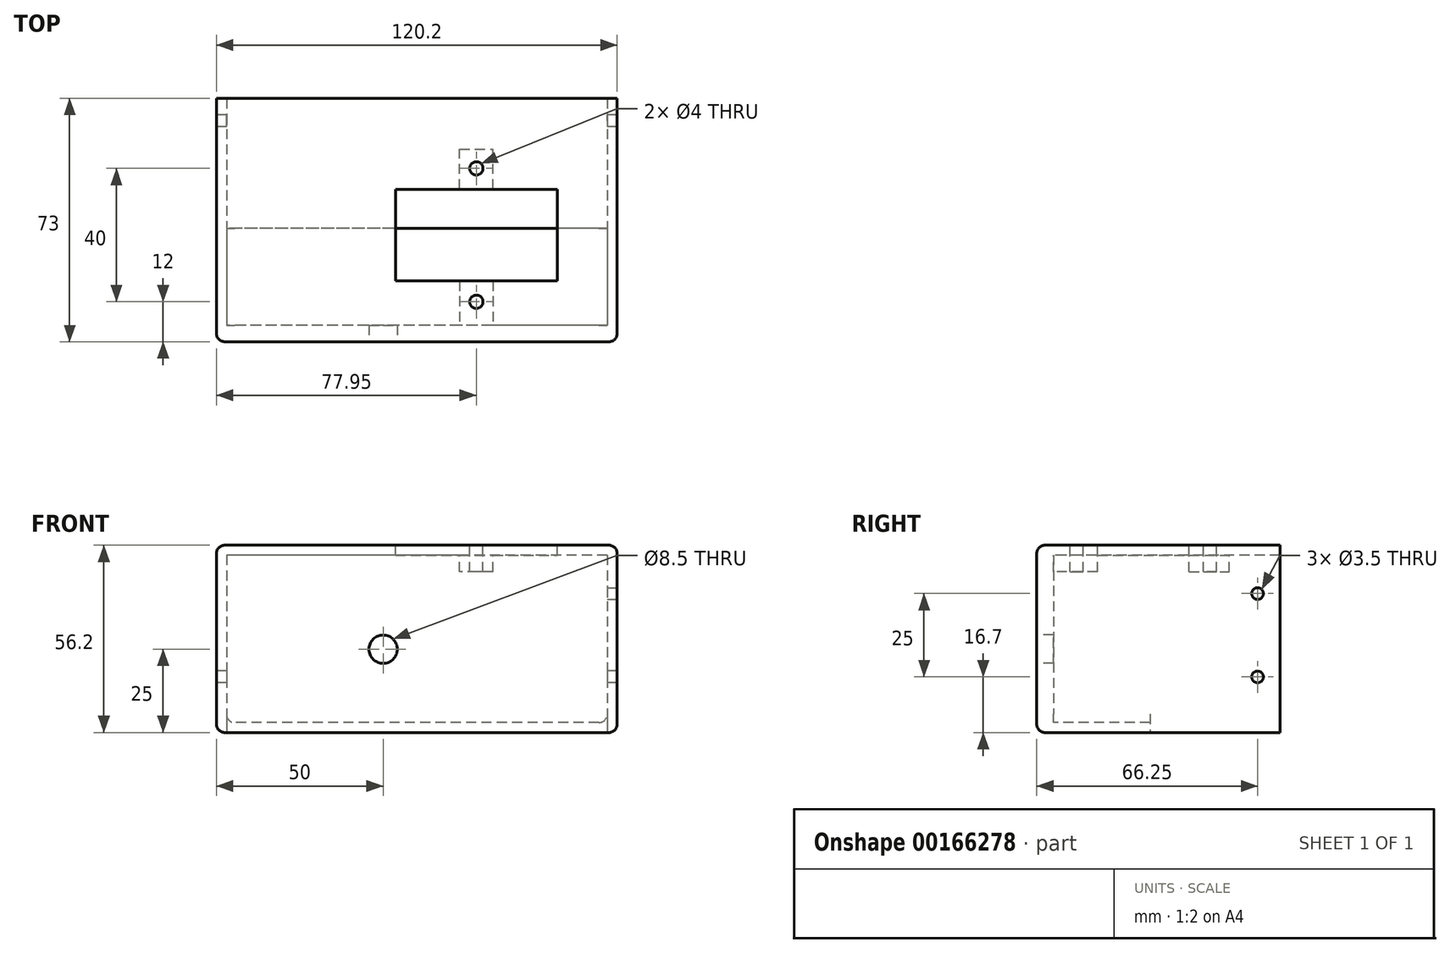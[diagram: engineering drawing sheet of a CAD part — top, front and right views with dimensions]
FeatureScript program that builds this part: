
annotation { "Feature Type Name" : "Feature", "Feature Type Description" : "" }
export const myFeature = defineFeature(function(context is Context, id is Id, definition is map)
    precondition{}
    {
        {
            var Q0;
            Q0=qCreatedBy(makeId("Front.planeOp"),FACE);
            var sketch = newSketch(context, id + "F0", { "sketchPlane" : qUnion([Q0])});
            skLineSegment(sketch, "E0.bottom", {"start": v(60.1, 28.1) * mm, "end": v(-60.1, 28.1) * mm});
            skLineSegment(sketch, "E0.top", {"start": v(60.1, -28.1) * mm, "end": v(-60.1, -28.1) * mm});
            skLineSegment(sketch, "E0.left", {"start": v(60.1, 28.1) * mm, "end": v(60.1, -28.1) * mm});
            skLineSegment(sketch, "E0.right", {"start": v(-60.1, 28.1) * mm, "end": v(-60.1, -28.1) * mm});
            skPoint(sketch, "E0.middle", {"position": v(0, 0) * mm});
            skCircle(sketch, "E1", {"center": v(-10.1, -3.1) * mm, "radius": 4.25 * mm});
            skSolve(sketch);
        }
        {
            var Q0;
            Q0=makeQuery(id+"F0.imprint","IMPRINT",FACE,{"disambiguationData":[TD([[makeQuery(id+"F0.imprint","IMPRINT",EDGE,{"derivedFrom":sQuery(id+"F0.wireOp",EDGE,"E0.bottom")}),1.0]])]});
            extrude(context, id + "F1", {"entities" : qUnion([Q0]), "oppositeDirection" : true, "depth" : 5 * mm});
        }
        {
            var Q0;
            Q0=makeQuery(id+"F1.opExtrude","CAP_FACE",FACE,{"disambiguationData":[OSD([sQuery(id+"F0.wireOp",EDGE,"E0.bottom"),sQuery(id+"F0.wireOp",EDGE,"E0.top"),sQuery(id+"F0.wireOp",EDGE,"E0.left"),sQuery(id+"F0.wireOp",EDGE,"E0.right"),sQuery(id+"F0.wireOp",EDGE,"E1")])],"isStart":false});
            var sketch = newSketch(context, id + "F2", { "sketchPlane" : qUnion([Q0])});
            skLineSegment(sketch, "E2.0", {"start": v(-60.1, 28.1) * mm, "end": v(60.1, 28.1) * mm});
            skLineSegment(sketch, "E3.0", {"start": v(-60.1, 28.1) * mm, "end": v(-60.1, -28.1) * mm});
            skLineSegment(sketch, "E4.0", {"start": v(-60.1, -28.1) * mm, "end": v(60.1, -28.1) * mm});
            skLineSegment(sketch, "E5.0", {"start": v(60.1, 28.1) * mm, "end": v(60.1, -28.1) * mm});
            skLineSegment(sketch, "E6.0", {"start": v(-57.1, 25.1) * mm, "end": v(57.1, 25.1) * mm});
            skLineSegment(sketch, "E6.1", {"start": v(-57.1, 25.1) * mm, "end": v(-57.1, -25.1) * mm});
            skLineSegment(sketch, "E6.2", {"start": v(-57.1, -25.1) * mm, "end": v(57.1, -25.1) * mm});
            skLineSegment(sketch, "E6.3", {"start": v(57.1, 25.1) * mm, "end": v(57.1, -25.1) * mm});
            skSolve(sketch);
        }
        {
            var Q0;
            Q0=makeQuery(id+"F2.imprint","IMPRINT",FACE,{"disambiguationData":[TD([[makeQuery(id+"F2.imprint","IMPRINT",EDGE,{"derivedFrom":sQuery(id+"F2.wireOp",EDGE,"E2.0")}),-1.0]])]});
            extrude(context, id + "F3", {"entities" : qUnion([Q0]), "operationType" : NewBodyOperationType.ADD, "depth" : (60 + 3 + 5) * mm});
        }
        {
            var Q0;
            Q0=makeQuery(id+"F3.boolean.opBoolean","MERGE",FACE,{"derivedFrom":[makeQuery(id+"F1.opExtrude","SWEPT_FACE",FACE,{"disambiguationData":[OSD([sQuery(id+"F0.wireOp",EDGE,"E0.bottom")])]}),makeQuery(id+"F3.opExtrude","SWEPT_FACE",FACE,{"disambiguationData":[OSD([sQuery(id+"F2.wireOp",EDGE,"E2.0")])]})]});
            var sketch = newSketch(context, id + "F4", { "sketchPlane" : qUnion([Q0])});
            skLineSegment(sketch, "E7.bottom", {"start": v(-6.4, 18.25) * mm, "end": v(42.1, 18.25) * mm});
            skLineSegment(sketch, "E7.top", {"start": v(-6.4, 45.75) * mm, "end": v(42.1, 45.75) * mm});
            skLineSegment(sketch, "E7.left", {"start": v(-6.4, 18.25) * mm, "end": v(-6.4, 45.75) * mm});
            skLineSegment(sketch, "E7.right", {"start": v(42.1, 18.25) * mm, "end": v(42.1, 45.75) * mm});
            skPoint(sketch, "E7.middle", {"position": v(17.85, 32) * mm});
            skCircle(sketch, "E8", {"center": v(17.85, 52) * mm, "radius": 2 * mm});
            skCircle(sketch, "E9", {"center": v(17.85, 12) * mm, "radius": 2 * mm});
            skLineSegment(sketch, "E10", {"start": v(17.85, 12) * mm, "end": v(17.85, 52) * mm, "construction": true});
            skLineSegment(sketch, "E11", {"start": v(42.1, 32) * mm, "end": v(-6.4, 32) * mm, "construction": true});
            skLineSegment(sketch, "E12.0", {"start": v(57.1, 5) * mm, "end": v(-57.1, 5) * mm, "construction": true});
            skLineSegment(sketch, "E13.0", {"start": v(57.1, 73) * mm, "end": v(57.1, 5) * mm, "construction": true});
            skSolve(sketch);
        }
        {
            var Q0;
            Q0 = qSketchRegion(id + "F4", true);
            extrude(context, id + "F5", {"entities" : qUnion([Q0]), "operationType" : NewBodyOperationType.REMOVE, "oppositeDirection" : true, "depth" : 25 * mm});
        }
        {
            var Q0;
            Q0=makeQuery(id+"F3.boolean.opBoolean","MERGE",FACE,{"derivedFrom":[makeQuery(id+"F1.opExtrude","SWEPT_FACE",FACE,{"disambiguationData":[OSD([sQuery(id+"F0.wireOp",EDGE,"E0.right")])]}),makeQuery(id+"F3.opExtrude","SWEPT_FACE",FACE,{"disambiguationData":[OSD([sQuery(id+"F2.wireOp",EDGE,"E5.0")])]})]});
            var sketch = newSketch(context, id + "F6", { "sketchPlane" : qUnion([Q0])});
            skLineSegment(sketch, "E14.0", {"start": v(-73, 25.1) * mm, "end": v(-5, 25.1) * mm, "construction": true});
            skCircle(sketch, "E15", {"center": v(-66.25, -11.4) * mm, "radius": 1.75 * mm});
            skSolve(sketch);
        }
        {
            var Q0;
            Q0=makeQuery(id+"F6.imprint","IMPRINT",FACE,{"disambiguationData":[TD([[makeQuery(id+"F6.imprint","IMPRINT",EDGE,{"derivedFrom":sQuery(id+"F6.wireOp",EDGE,"E15")}),1.0]])]});
            extrude(context, id + "F7", {"entities" : qUnion([Q0]), "operationType" : NewBodyOperationType.REMOVE, "endBound" : BoundingType.THROUGH_ALL, "oppositeDirection" : true, "depth" : 25 * mm});
        }
        {
            var Q0;
            Q0=makeQuery(id+"F3.boolean.opBoolean","MERGE",FACE,{"derivedFrom":[makeQuery(id+"F1.opExtrude","SWEPT_FACE",FACE,{"disambiguationData":[OSD([sQuery(id+"F0.wireOp",EDGE,"E0.left")])]}),makeQuery(id+"F3.opExtrude","SWEPT_FACE",FACE,{"disambiguationData":[OSD([sQuery(id+"F2.wireOp",EDGE,"E3.0")])]})]});
            var sketch = newSketch(context, id + "F8", { "sketchPlane" : qUnion([Q0])});
            skCircle(sketch, "E16.0", {"center": v(66.25, -11.4) * mm, "radius": 1.75 * mm, "construction": true});
            skLineSegment(sketch, "E17", {"start": v(66.25, -11.4) * mm, "end": v(66.25, 28.1) * mm, "construction": true});
            skLineSegment(sketch, "E18.0", {"start": v(73, 25.1) * mm, "end": v(5, 25.1) * mm, "construction": true});
            skCircle(sketch, "E19", {"center": v(66.25, 13.6) * mm, "radius": 1.75 * mm});
            skSolve(sketch);
        }
        {
            var Q0;
            Q0=makeQuery(id+"F8.imprint","IMPRINT",FACE,{"disambiguationData":[TD([[makeQuery(id+"F8.imprint","IMPRINT",EDGE,{"derivedFrom":sQuery(id+"F8.wireOp",EDGE,"E19")}),1.0]])]});
            var Q1;
            Q1=makeQuery(id+"F3.opExtrude","SWEPT_FACE",FACE,{"disambiguationData":[OSD([sQuery(id+"F2.wireOp",EDGE,"E6.1")])]});
            extrude(context, id + "F9", {"entities" : qUnion([Q0]), "operationType" : NewBodyOperationType.REMOVE, "endBound" : BoundingType.UP_TO_SURFACE, "oppositeDirection" : true, "endBoundEntityFace" : qUnion([Q1]), "depth" : 25 * mm});
        }
        {
            var Q0;
            Q0=makeQuery(id+"F3.boolean.opBoolean","MERGE",FACE,{"derivedFrom":[makeQuery(id+"F1.opExtrude","SWEPT_FACE",FACE,{"disambiguationData":[OSD([sQuery(id+"F0.wireOp",EDGE,"E0.top")])]}),makeQuery(id+"F3.opExtrude","SWEPT_FACE",FACE,{"disambiguationData":[OSD([sQuery(id+"F2.wireOp",EDGE,"E4.0")])]})]});
            var sketch = newSketch(context, id + "F10", { "sketchPlane" : qUnion([Q0])});
            skLineSegment(sketch, "E20.0", {"start": v(57.1, -73) * mm, "end": v(57.1, -34) * mm});
            skLineSegment(sketch, "E21.0", {"start": v(-57.1, -73) * mm, "end": v(-57.1, -34) * mm});
            skLineSegment(sketch, "E22", {"start": v(57.1, -34) * mm, "end": v(-57.1, -34) * mm});
            skLineSegment(sketch, "E23", {"start": v(-57.1, -73) * mm, "end": v(57.1, -73) * mm});
            skPoint(sketch, "E24.orphan", {"position": v(57.1, -5) * mm});
            skPoint(sketch, "E25.orphan", {"position": v(-57.1, -5) * mm});
            skSolve(sketch);
        }
        {
            var Q0;
            Q0=makeQuery(id+"F10.imprint","IMPRINT",FACE,{"disambiguationData":[TD([[makeQuery(id+"F10.imprint","IMPRINT",EDGE,{"derivedFrom":sQuery(id+"F10.wireOp",EDGE,"E20.0")}),1.0]])]});
            var Q1;
            Q1=makeQuery(id+"F3.opExtrude","SWEPT_FACE",FACE,{"disambiguationData":[OSD([sQuery(id+"F2.wireOp",EDGE,"E6.2")])]});
            extrude(context, id + "F11", {"entities" : qUnion([Q0]), "operationType" : NewBodyOperationType.REMOVE, "endBound" : BoundingType.UP_TO_SURFACE, "oppositeDirection" : true, "endBoundEntityFace" : qUnion([Q1]), "depth" : 25 * mm});
        }
        {
            var Q0;
            Q0=makeQuery(id+"F3.boolean.opBoolean","MERGE",FACE,{"derivedFrom":[makeQuery(id+"F1.opExtrude","SWEPT_FACE",FACE,{"disambiguationData":[OSD([sQuery(id+"F0.wireOp",EDGE,"E0.bottom")])]}),makeQuery(id+"F3.opExtrude","SWEPT_FACE",FACE,{"disambiguationData":[OSD([sQuery(id+"F2.wireOp",EDGE,"E2.0")])]})]});
            var sketch = newSketch(context, id + "F12", { "sketchPlane" : qUnion([Q0])});
            skText(sketch, "E26", { "text": "TJL Engineering", "fontName": "RobotoSlab-Bold.ttf"});
            const initialGuessF12  = {"E26": [-0.0551, -0.0231, 1, 0, 0.00546]};
            skSetInitialGuess(sketch, initialGuessF12);
            skSolve(sketch);
        }
        {
            var Q0;
            Q0 = qSketchRegion(id + "F12", true);
            extrude(context, id + "F13", {"entities" : qUnion([Q0]), "operationType" : NewBodyOperationType.REMOVE, "oppositeDirection" : true, "depth" : 2 * mm});
        }
        {
            var Q0;
            Q0=makeQuery(id+"F3.opExtrude","SWEPT_FACE",FACE,{"disambiguationData":[OSD([sQuery(id+"F2.wireOp",EDGE,"E6.0")])]});
            var sketch = newSketch(context, id + "F14", { "sketchPlane" : qUnion([Q0])});
            skCircle(sketch, "E27.0", {"center": v(17.85, -52) * mm, "radius": 2 * mm, "construction": true});
            skCircle(sketch, "E27.1", {"center": v(17.85, -12) * mm, "radius": 2 * mm, "construction": true});
            skLineSegment(sketch, "E28", {"start": v(-6.4, -32) * mm, "end": v(42.1, -32) * mm, "construction": true});
            skLineSegment(sketch, "E29", {"start": v(17.85, -45.75) * mm, "end": v(17.85, -57.75) * mm, "construction": true});
            skLineSegment(sketch, "E30.0", {"start": v(12.85, -45.75) * mm, "end": v(12.85, -57.75) * mm});
            skLineSegment(sketch, "E31.0", {"start": v(22.85, -45.75) * mm, "end": v(22.85, -57.75) * mm});
            skLineSegment(sketch, "E32", {"start": v(12.85, -57.75) * mm, "end": v(22.85, -57.75) * mm});
            skLineSegment(sketch, "E33.MirrorCS", {"start": v(12.85, -18.25) * mm, "end": v(12.85, -6.25) * mm});
            skLineSegment(sketch, "E34.MirrorCS", {"start": v(17.85, -18.25) * mm, "end": v(17.85, -6.25) * mm, "construction": true});
            skLineSegment(sketch, "E35.MirrorCS", {"start": v(22.85, -18.25) * mm, "end": v(22.85, -6.25) * mm});
            skLineSegment(sketch, "E36", {"start": v(12.85, -45.75) * mm, "end": v(22.85, -45.75) * mm});
            skLineSegment(sketch, "E37", {"start": v(12.85, -18.25) * mm, "end": v(22.85, -18.25) * mm});
            skLineSegment(sketch, "E38", {"start": v(12.85, -6.25) * mm, "end": v(12.85, -5) * mm});
            skLineSegment(sketch, "E39", {"start": v(12.85, -5) * mm, "end": v(22.85, -5) * mm});
            skLineSegment(sketch, "E40", {"start": v(22.85, -5) * mm, "end": v(22.85, -6.25) * mm});
            skCircle(sketch, "E41", {"center": v(17.85, -52) * mm, "radius": 1.9 * mm});
            skCircle(sketch, "E42", {"center": v(17.85, -12) * mm, "radius": 1.9 * mm});
            skSolve(sketch);
        }
        {
            var Q0;
            Q0=makeQuery(id+"F14.imprint","IMPRINT",FACE,{"disambiguationData":[TD([[makeQuery(id+"F14.imprint","IMPRINT",EDGE,{"derivedFrom":sQuery(id+"F14.wireOp",EDGE,"E30.0")}),1.0]])]});
            var Q1;
            Q1=makeQuery(id+"F14.imprint","IMPRINT",FACE,{"disambiguationData":[TD([[makeQuery(id+"F14.imprint","IMPRINT",EDGE,{"derivedFrom":sQuery(id+"F14.wireOp",EDGE,"E33.MirrorCS")}),-1.0]])]});
            extrude(context, id + "F15", {"entities" : qUnion([Q0, Q1]), "operationType" : NewBodyOperationType.ADD, "depth" : 5 * mm});
        }
        {
            var Q0;
            Q0=makeQuery(id+"F3.boolean.opBoolean","MERGE",EDGE,{"derivedFrom":[makeQuery(id+"F1.opExtrude","SWEPT_EDGE",EDGE,{"disambiguationData":[OSD([sQuery(id+"F0.wireOp",EDGE,"E0.bottom"),sQuery(id+"F0.wireOp",EDGE,"E0.right")])]}),makeQuery(id+"F3.opExtrude","SWEPT_EDGE",EDGE,{"disambiguationData":[OSD([sQuery(id+"F2.wireOp",EDGE,"E2.0"),sQuery(id+"F2.wireOp",EDGE,"E5.0")])]})]});
            var Q1;
            Q1=makeQuery(id+"F3.boolean.opBoolean","MERGE",EDGE,{"derivedFrom":[makeQuery(id+"F1.opExtrude","SWEPT_EDGE",EDGE,{"disambiguationData":[OSD([sQuery(id+"F0.wireOp",EDGE,"E0.top"),sQuery(id+"F0.wireOp",EDGE,"E0.right")])]}),makeQuery(id+"F3.opExtrude","SWEPT_EDGE",EDGE,{"disambiguationData":[OSD([sQuery(id+"F2.wireOp",EDGE,"E4.0"),sQuery(id+"F2.wireOp",EDGE,"E5.0")])]})]});
            var Q2;
            Q2=makeQuery(id+"F3.boolean.opBoolean","MERGE",EDGE,{"derivedFrom":[makeQuery(id+"F1.opExtrude","SWEPT_EDGE",EDGE,{"disambiguationData":[OSD([sQuery(id+"F0.wireOp",EDGE,"E0.bottom"),sQuery(id+"F0.wireOp",EDGE,"E0.left")])]}),makeQuery(id+"F3.opExtrude","SWEPT_EDGE",EDGE,{"disambiguationData":[OSD([sQuery(id+"F2.wireOp",EDGE,"E2.0"),sQuery(id+"F2.wireOp",EDGE,"E3.0")])]})]});
            var Q3;
            Q3=makeQuery(id+"F3.boolean.opBoolean","MERGE",EDGE,{"derivedFrom":[makeQuery(id+"F1.opExtrude","SWEPT_EDGE",EDGE,{"disambiguationData":[OSD([sQuery(id+"F0.wireOp",EDGE,"E0.top"),sQuery(id+"F0.wireOp",EDGE,"E0.left")])]}),makeQuery(id+"F3.opExtrude","SWEPT_EDGE",EDGE,{"disambiguationData":[OSD([sQuery(id+"F2.wireOp",EDGE,"E3.0"),sQuery(id+"F2.wireOp",EDGE,"E4.0")])]})]});
            var Q4;
            Q4=makeQuery(id+"F1.opExtrude","CAP_EDGE",EDGE,{"disambiguationData":[OSD([sQuery(id+"F0.wireOp",EDGE,"E0.left")])],"isStart":true});
            var Q5;
            Q5=makeQuery(id+"F1.opExtrude","CAP_EDGE",EDGE,{"disambiguationData":[OSD([sQuery(id+"F0.wireOp",EDGE,"E0.bottom")])],"isStart":true});
            var Q6;
            Q6=makeQuery(id+"F1.opExtrude","CAP_EDGE",EDGE,{"disambiguationData":[OSD([sQuery(id+"F0.wireOp",EDGE,"E0.top")])],"isStart":true});
            var Q7;
            Q7=makeQuery(id+"F1.opExtrude","CAP_EDGE",EDGE,{"disambiguationData":[OSD([sQuery(id+"F0.wireOp",EDGE,"E0.right")])],"isStart":true});
            var Q8;
            Q8=makeQuery(id+"F3.opExtrude","CAP_EDGE",EDGE,{"disambiguationData":[OSD([sQuery(id+"F2.wireOp",EDGE,"E6.3")])],"isStart":true});
            var Q9;
            Q9=makeQuery(id+"F3.opExtrude","CAP_EDGE",EDGE,{"disambiguationData":[OSD([sQuery(id+"F2.wireOp",EDGE,"E6.1")])],"isStart":true});
            var Q10;
            Q10=makeQuery(id+"F3.opExtrude","CAP_EDGE",EDGE,{"disambiguationData":[OSD([sQuery(id+"F2.wireOp",EDGE,"E6.2")])],"isStart":true});
            var Q11;
            Q11=makeQuery(id+"F3.opExtrude","SWEPT_EDGE",EDGE,{"disambiguationData":[OSD([sQuery(id+"F2.wireOp",EDGE,"E6.2"),sQuery(id+"F2.wireOp",EDGE,"E6.3")])]});
            var Q12;
            Q12=makeQuery(id+"F3.opExtrude","SWEPT_EDGE",EDGE,{"disambiguationData":[OSD([sQuery(id+"F2.wireOp",EDGE,"E6.1"),sQuery(id+"F2.wireOp",EDGE,"E6.2")])]});
            var Q13;
            Q13=makeQuery(id+"F15.opExtrude","CAP_EDGE",EDGE,{"disambiguationData":[OSD([sQuery(id+"F14.wireOp",EDGE,"E39")])],"isStart":false});
            var Q14;
            {var subQ0=sQuery(id+"F2.wireOp",EDGE,"E6.0");Q14=makeQuery(id+"F15.boolean.opBoolean","SPLIT",EDGE,{"disambiguationData":[TD([makeQuery(id+"F3.opExtrude","SWEPT_FACE",FACE,{"disambiguationData":[OSD([sQuery(id+"F2.wireOp",EDGE,"E6.3")])]})])],"derivedFrom":makeQuery(id+"F3.opExtrude","CAP_EDGE",EDGE,{"disambiguationData":[OSD([subQ0])],"isStart":true})});}
            var Q15;
            {var subQ0=sQuery(id+"F2.wireOp",EDGE,"E6.0");Q15=makeQuery(id+"F15.boolean.opBoolean","SPLIT",EDGE,{"disambiguationData":[TD([makeQuery(id+"F3.opExtrude","SWEPT_FACE",FACE,{"disambiguationData":[OSD([sQuery(id+"F2.wireOp",EDGE,"E6.1")])]})])],"derivedFrom":makeQuery(id+"F3.opExtrude","CAP_EDGE",EDGE,{"disambiguationData":[OSD([subQ0])],"isStart":true})});}
            var Q16;
            Q16=makeQuery(id+"F15.opExtrude","SWEPT_EDGE",EDGE,{"disambiguationData":[OSD([sQuery(id+"F2.wireOp",EDGE,"E6.0"),sQuery(id+"F14.wireOp",EDGE,"E39"),sQuery(id+"F14.wireOp",EDGE,"E40")])]});
            var Q17;
            Q17=makeQuery(id+"F15.opExtrude","SWEPT_EDGE",EDGE,{"disambiguationData":[OSD([sQuery(id+"F2.wireOp",EDGE,"E6.0"),sQuery(id+"F14.wireOp",EDGE,"E38"),sQuery(id+"F14.wireOp",EDGE,"E39")])]});
            fillet(context, id + "F16", {"entities" : qUnion([Q0, Q1, Q2, Q3, Q4, Q5, Q6, Q7, Q8, Q9, Q10, Q11, Q12, Q13, Q14, Q15, Q16, Q17]), "radius" : 2.5 * mm, "tangentPropagation" : true, "allowEdgeOverflow" : false});
        }
    });
